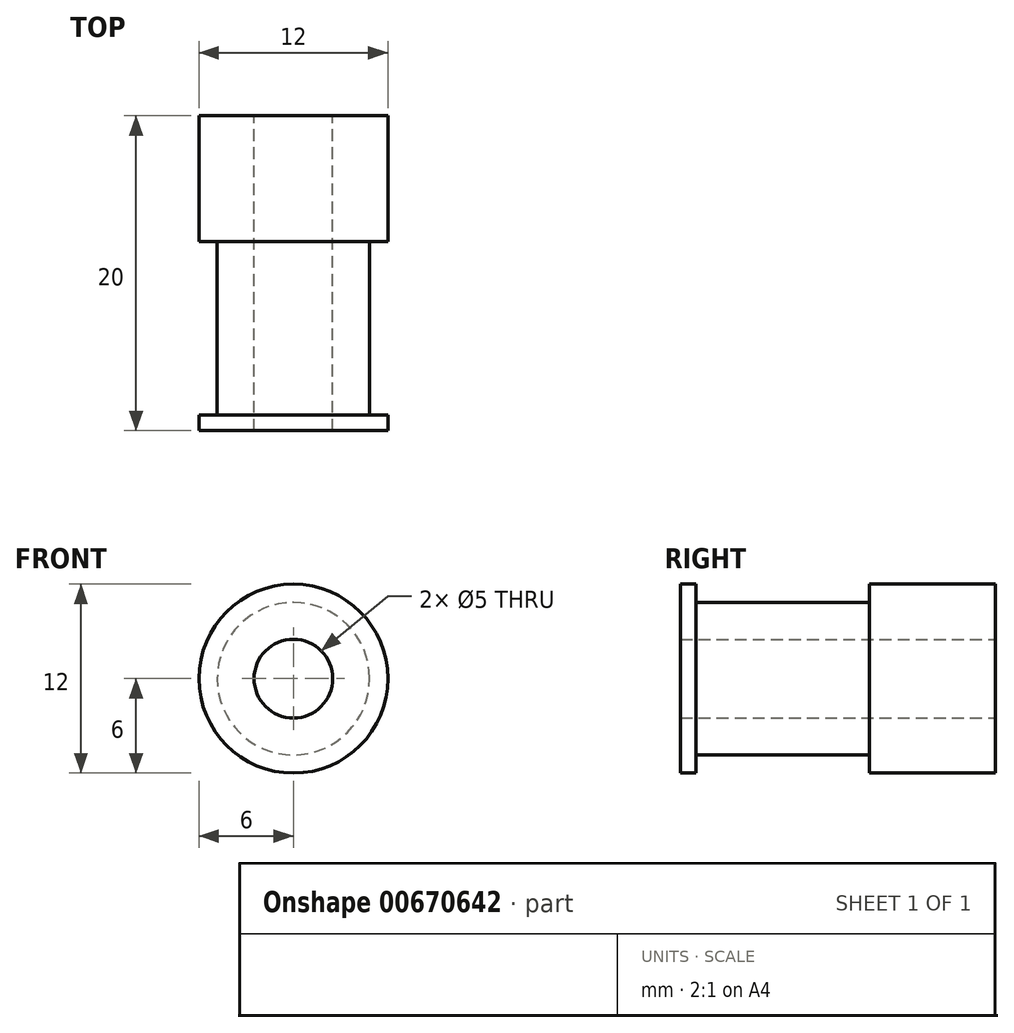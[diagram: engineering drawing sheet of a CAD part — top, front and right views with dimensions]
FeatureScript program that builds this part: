
annotation { "Feature Type Name" : "Feature", "Feature Type Description" : "" }
export const myFeature = defineFeature(function(context is Context, id is Id, definition is map)
    precondition{}
    {
        {
            var Q0;
            Q0=qCreatedBy(makeId("Front.planeOp"),FACE);
            var sketch = newSketch(context, id + "F0", { "sketchPlane" : qUnion([Q0])});
            skCircle(sketch, "E0", {"center": v(0, 0) * mm, "radius": 6 * mm});
            skCircle(sketch, "E1", {"center": v(0, 0) * mm, "radius": 2.5 * mm});
            skSolve(sketch);
        }
        {
            var Q0;
            Q0 = qSketchRegion(id + "F0", true);
            extrude(context, id + "F1", {"entities" : qUnion([Q0]), "endBound" : BoundingType.SYMMETRIC, "depth" : 20 * mm, "offsetDistance" : 25 * mm});
        }
        {
            var Q0;
            Q0=makeQuery(id+"F1.opExtrude","CAP_FACE",FACE,{"disambiguationData":[OSD([sQuery(id+"F0.wireOp",EDGE,"E0"),sQuery(id+"F0.wireOp",EDGE,"E1")])],"isStart":false});
            cPlane(context, id + "F2", {"entities" : qUnion([Q0]), "cplaneType" : CPlaneType.OFFSET, "offset" : 1 * mm, "oppositeDirection" : true, "width" : 150 * mm, "height" : 150 * mm});
        }
        {
            var Q0;
            Q0=qCreatedBy(id+"F2.planeOp",FACE);
            var sketch = newSketch(context, id + "F3", { "sketchPlane" : qUnion([Q0])});
            skCircle(sketch, "E2", {"center": v(0, 0) * mm, "radius": 4.84 * mm});
            skCircle(sketch, "E3", {"center": v(0, 0) * mm, "radius": 7 * mm});
            skSolve(sketch);
        }
        {
            var Q0;
            Q0 = qSketchRegion(id + "F3", true);
            extrude(context, id + "F4", {"entities" : qUnion([Q0]), "operationType" : NewBodyOperationType.REMOVE, "oppositeDirection" : true, "depth" : 11 * mm, "offsetDistance" : 25 * mm});
        }
    });
